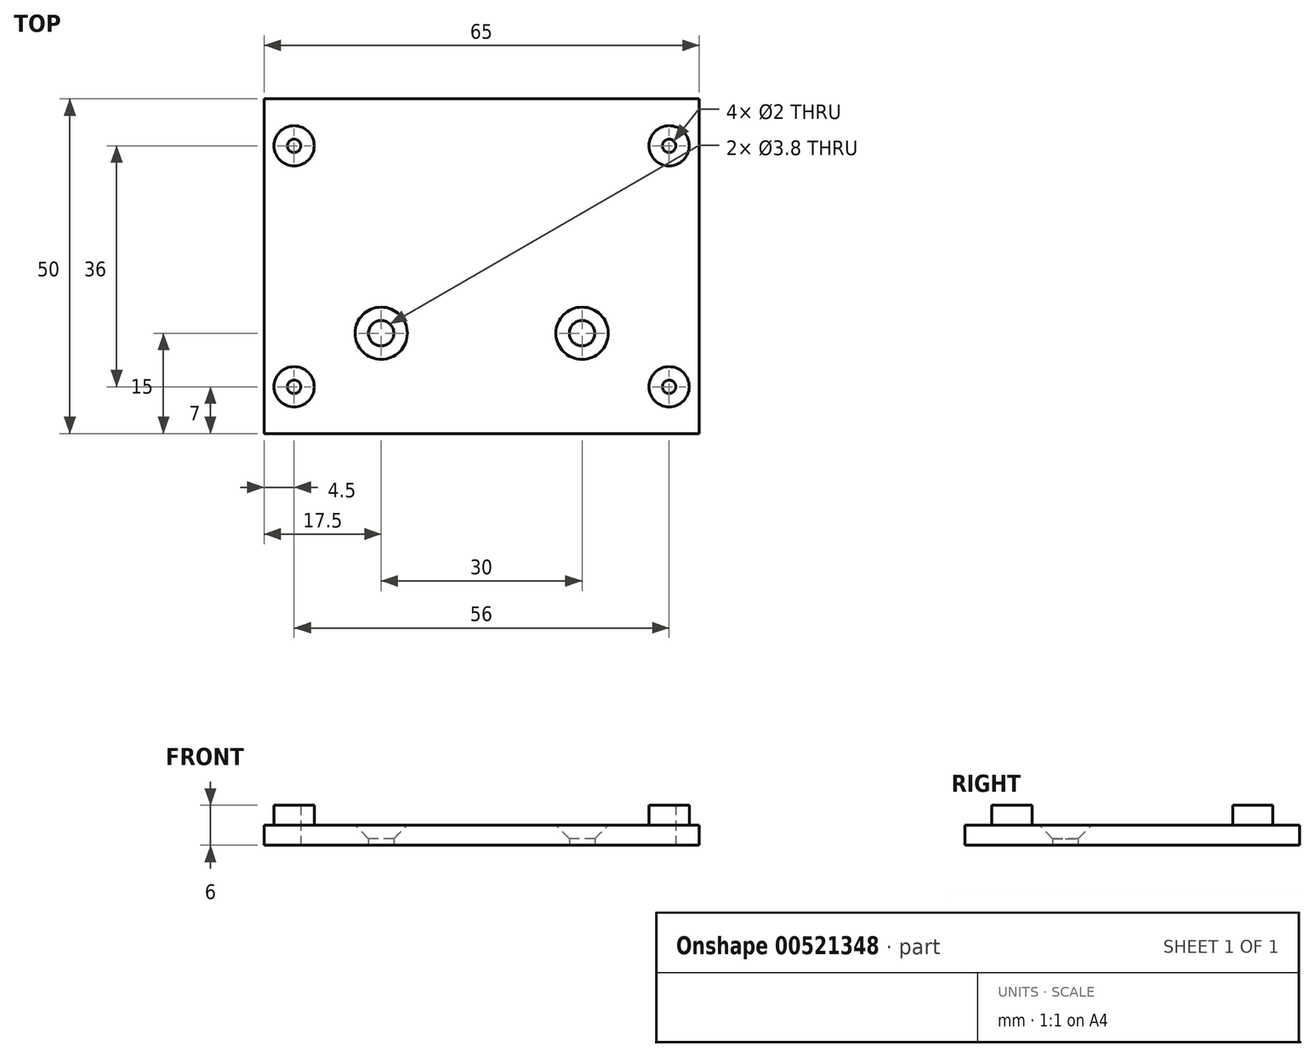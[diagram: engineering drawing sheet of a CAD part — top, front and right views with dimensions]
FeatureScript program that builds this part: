
annotation { "Feature Type Name" : "Feature", "Feature Type Description" : "" }
export const myFeature = defineFeature(function(context is Context, id is Id, definition is map)
    precondition{}
    {
        {
            var Q0;
            Q0=qCreatedBy(makeId("Top.planeOp"),FACE);
            var sketch = newSketch(context, id + "F0", { "sketchPlane" : qUnion([Q0])});
            skLineSegment(sketch, "E0.bottom", {"start": v(0, 0) * mm, "end": v(65, 0) * mm});
            skLineSegment(sketch, "E0.top", {"start": v(0, 50) * mm, "end": v(65, 50) * mm});
            skLineSegment(sketch, "E0.left", {"start": v(0, 0) * mm, "end": v(0, 50) * mm});
            skLineSegment(sketch, "E0.right", {"start": v(65, 0) * mm, "end": v(65, 50) * mm});
            skLineSegment(sketch, "E1", {"start": v(32.5, 50) * mm, "end": v(32.5, 0) * mm, "construction": true});
            skLineSegment(sketch, "E2", {"start": v(0, 25) * mm, "end": v(65, 25) * mm, "construction": true});
            skCircle(sketch, "E3", {"center": v(4.5, 43) * mm, "radius": 1 * mm});
            skCircle(sketch, "E4.MirrorC", {"center": v(60.5, 43) * mm, "radius": 1 * mm});
            skCircle(sketch, "E5.MirrorC", {"center": v(4.5, 7) * mm, "radius": 1 * mm});
            skCircle(sketch, "E6.MirrorC", {"center": v(60.5, 7) * mm, "radius": 1 * mm});
            skCircle(sketch, "E7", {"center": v(17.5, 15) * mm, "radius": 1.9 * mm});
            skCircle(sketch, "E8.MirrorC", {"center": v(47.5, 15) * mm, "radius": 1.9 * mm});
            skSolve(sketch);
        }
        {
            var Q0;
            Q0 = qSketchRegion(id + "F0", true);
            extrude(context, id + "F1", {"entities" : qUnion([Q0]), "depth" : 3 * mm, "offsetDistance" : 25 * mm});
        }
        {
            var Q0;
            Q0=makeQuery(id+"F1.opExtrude","CAP_EDGE",EDGE,{"disambiguationData":[OSD([sQuery(id+"F0.wireOp",EDGE,"E7")])],"isStart":false});
            var Q1;
            Q1=makeQuery(id+"F1.opExtrude","CAP_EDGE",EDGE,{"disambiguationData":[OSD([sQuery(id+"F0.wireOp",EDGE,"E8.MirrorC")])],"isStart":false});
            chamfer(context, id + "F2", {"entities" : qUnion([Q0, Q1]), "width" : 2 * mm, "tangentPropagation" : true});
        }
        {
            var Q0;
            Q0=makeQuery(id+"F1.opExtrude","CAP_FACE",FACE,{"disambiguationData":[OSD([sQuery(id+"F0.wireOp",EDGE,"E0.bottom"),sQuery(id+"F0.wireOp",EDGE,"E0.top"),sQuery(id+"F0.wireOp",EDGE,"E0.left"),sQuery(id+"F0.wireOp",EDGE,"E0.right"),sQuery(id+"F0.wireOp",EDGE,"E3"),sQuery(id+"F0.wireOp",EDGE,"E4.MirrorC"),sQuery(id+"F0.wireOp",EDGE,"E5.MirrorC"),sQuery(id+"F0.wireOp",EDGE,"E6.MirrorC"),sQuery(id+"F0.wireOp",EDGE,"E7"),sQuery(id+"F0.wireOp",EDGE,"E8.MirrorC")])],"isStart":false});
            var sketch = newSketch(context, id + "F3", { "sketchPlane" : qUnion([Q0])});
            skCircle(sketch, "E9.0", {"center": v(4.5, 43) * mm, "radius": 1 * mm});
            skCircle(sketch, "E10.0", {"center": v(60.5, 43) * mm, "radius": 1 * mm});
            skCircle(sketch, "E11.0", {"center": v(60.5, 7) * mm, "radius": 1 * mm});
            skCircle(sketch, "E12.0", {"center": v(4.5, 7) * mm, "radius": 1 * mm});
            skCircle(sketch, "E13.0", {"center": v(4.5, 43) * mm, "radius": 3 * mm});
            skCircle(sketch, "E14.0", {"center": v(60.5, 43) * mm, "radius": 3 * mm});
            skCircle(sketch, "E15.0", {"center": v(60.5, 7) * mm, "radius": 3 * mm});
            skCircle(sketch, "E16.0", {"center": v(4.5, 7) * mm, "radius": 3 * mm});
            skSolve(sketch);
        }
        {
            var Q0;
            Q0 = qSketchRegion(id + "F3", true);
            extrude(context, id + "F4", {"entities" : qUnion([Q0]), "operationType" : NewBodyOperationType.ADD, "depth" : 3 * mm, "offsetDistance" : 25 * mm});
        }
    });
